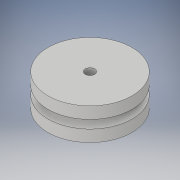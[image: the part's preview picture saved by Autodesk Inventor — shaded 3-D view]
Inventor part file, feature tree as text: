
AUTODESK INVENTOR PART (.ipt)
format: ipt  version: 2018 (Build 220112000, 112)  size: 131,072 bytes
history: native  units: in
note: dims shown in document units (in); Inventor stores cm internally (conversion verified against a paired STEP export)
features: sketch x2, revolve x1, extrude x1
ambient origin geometry x8: Origin, YZ Plane, XZ Plane, XY Plane, X Axis, Y Axis, Z Axis, Center Point
bodies: Solid1 (feature_tree)
feature tree (4):
  revolve  "Revolution1"  [1 undecoded]
  extrude  "Extrusion1"  TaperAngle=90.0deg  [1 undecoded]
  sketch  "Sketch1"  dims[d0=1.1in d1=0.834in]
  sketch  "Sketch2"  dims[d2=0.22in d3=90.0deg d4=0.25in d5=1.0in d6=0.0in]
note: 2 required parameter values undecoded (feature->parameter linkage not recoverable at this tier; creation-order binding heuristic only, values carry confidence <= 0.55)